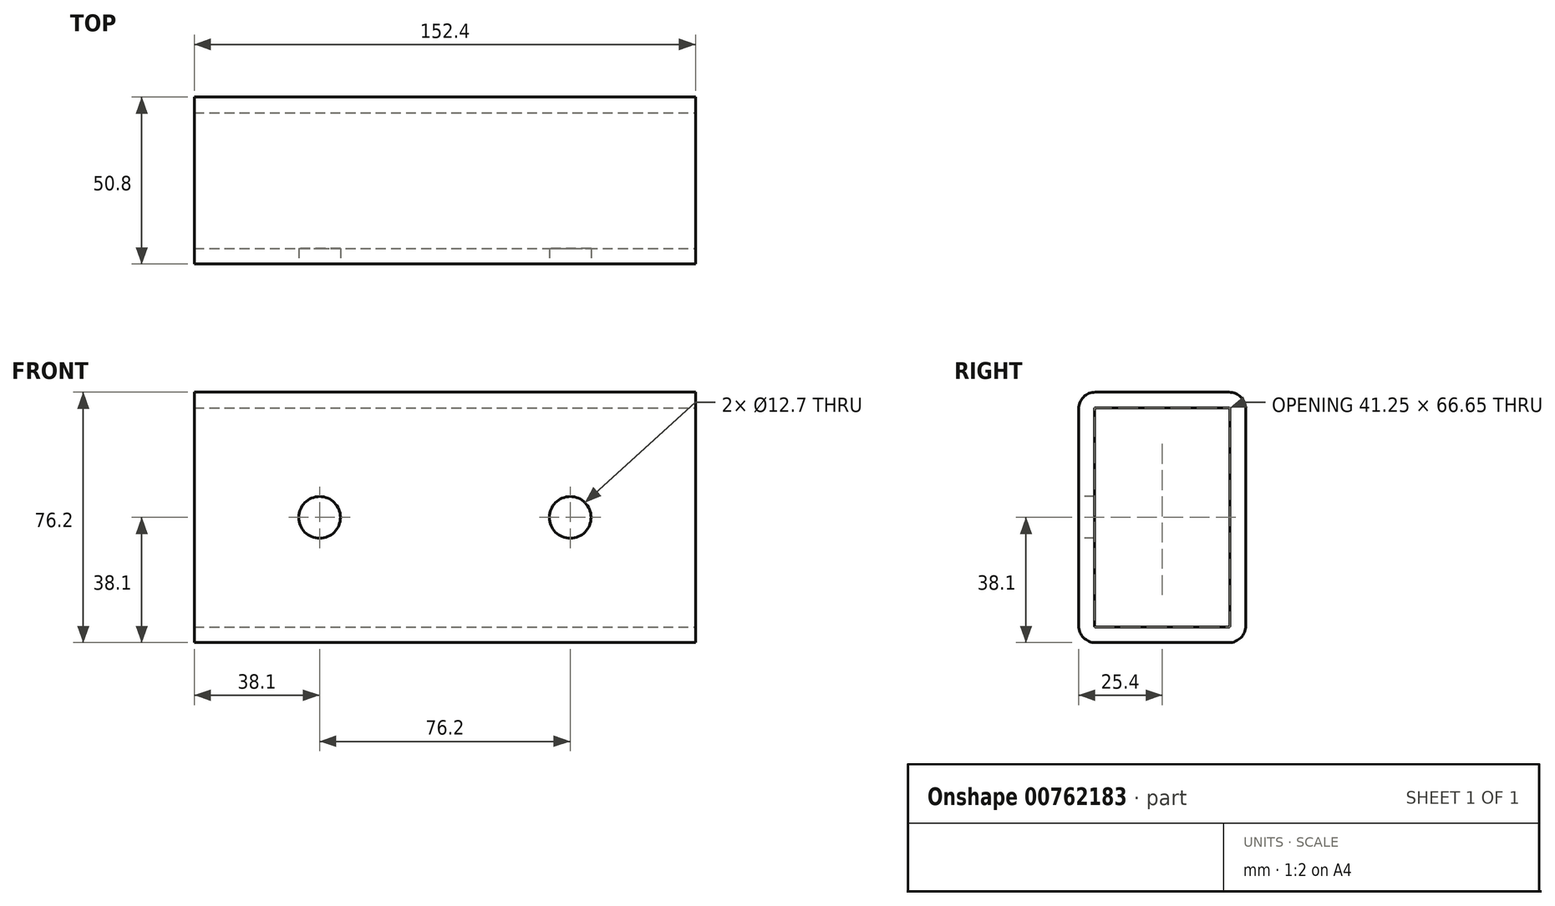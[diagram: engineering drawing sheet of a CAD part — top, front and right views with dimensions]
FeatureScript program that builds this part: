
annotation { "Feature Type Name" : "Feature", "Feature Type Description" : "" }
export const myFeature = defineFeature(function(context is Context, id is Id, definition is map)
    precondition{}
    {
        {
            var Q0;
            Q0=qCreatedBy(makeId("Right.planeOp"),FACE);
            var sketch = newSketch(context, id + "F0", { "sketchPlane" : qUnion([Q0])});
            skLineSegment(sketch, "E0.bottom", {"start": v(0, 0) * mm, "end": v(50.8, 0) * mm});
            skLineSegment(sketch, "E0.top", {"start": v(0, 76.2) * mm, "end": v(50.8, 76.2) * mm});
            skLineSegment(sketch, "E0.left", {"start": v(0, 0) * mm, "end": v(0, 76.2) * mm});
            skLineSegment(sketch, "E0.right", {"start": v(50.8, 0) * mm, "end": v(50.8, 76.2) * mm});
            skSolve(sketch);
        }
        {
            var Q0;
            Q0=makeQuery(id+"F0.imprint","IMPRINT",FACE,{"disambiguationData":[TD([[makeQuery(id+"F0.imprint","IMPRINT",EDGE,{"derivedFrom":sQuery(id+"F0.wireOp",EDGE,"E0.bottom")}),1.0]])]});
            extrude(context, id + "F1", {"entities" : qUnion([Q0]), "depth" : 152.4 * mm, "offsetDistance" : 25.4 * mm});
        }
        {
            var Q0;
            Q0=makeQuery(id+"F1.opExtrude","SWEPT_EDGE",EDGE,{"disambiguationData":[OSD([sQuery(id+"F0.wireOp",EDGE,"E0.top"),sQuery(id+"F0.wireOp",EDGE,"E0.left")])]});
            var Q1;
            Q1=makeQuery(id+"F1.opExtrude","SWEPT_EDGE",EDGE,{"disambiguationData":[OSD([sQuery(id+"F0.wireOp",EDGE,"E0.top"),sQuery(id+"F0.wireOp",EDGE,"E0.right")])]});
            var Q2;
            Q2=makeQuery(id+"F1.opExtrude","SWEPT_EDGE",EDGE,{"disambiguationData":[OSD([sQuery(id+"F0.wireOp",EDGE,"E0.bottom"),sQuery(id+"F0.wireOp",EDGE,"E0.left")])]});
            var Q3;
            Q3=makeQuery(id+"F1.opExtrude","SWEPT_EDGE",EDGE,{"disambiguationData":[OSD([sQuery(id+"F0.wireOp",EDGE,"E0.bottom"),sQuery(id+"F0.wireOp",EDGE,"E0.right")])]});
            fillet(context, id + "F2", {"entities" : qUnion([Q0, Q1, Q2, Q3]), "radius" : 5.08 * mm, "tangentPropagation" : true, "allowEdgeOverflow" : false});
        }
        {
            var Q0;
            Q0=makeQuery(id+"F1.opExtrude","CAP_FACE",FACE,{"disambiguationData":[OSD([sQuery(id+"F0.wireOp",EDGE,"E0.bottom"),sQuery(id+"F0.wireOp",EDGE,"E0.top"),sQuery(id+"F0.wireOp",EDGE,"E0.left"),sQuery(id+"F0.wireOp",EDGE,"E0.right")])],"isStart":false});
            var Q1;
            Q1=makeQuery(id+"F1.opExtrude","CAP_FACE",FACE,{"disambiguationData":[OSD([sQuery(id+"F0.wireOp",EDGE,"E0.bottom"),sQuery(id+"F0.wireOp",EDGE,"E0.top"),sQuery(id+"F0.wireOp",EDGE,"E0.left"),sQuery(id+"F0.wireOp",EDGE,"E0.right")])],"isStart":true});
            shell(context, id + "F3", {"entities" : qUnion([Q0, Q1]), "thickness" : 4.78 * mm});
        }
        {
            var Q0;
            Q0=makeQuery(id+"F1.opExtrude","SWEPT_FACE",FACE,{"disambiguationData":[OSD([sQuery(id+"F0.wireOp",EDGE,"E0.left")])]});
            var sketch = newSketch(context, id + "F4", { "sketchPlane" : qUnion([Q0])});
            skCircle(sketch, "E1", {"center": v(38.1, 38.1) * mm, "radius": 6.35 * mm});
            skPoint(sketch, "E1.centerSnap0", {"position": v(0, 38.1) * mm});
            skCircle(sketch, "E2", {"center": v(114.3, 38.1) * mm, "radius": 6.35 * mm});
            skSolve(sketch);
        }
        {
            var Q0;
            Q0=makeQuery(id+"F4.imprint","IMPRINT",FACE,{"disambiguationData":[TD([[makeQuery(id+"F4.imprint","IMPRINT",EDGE,{"derivedFrom":sQuery(id+"F4.wireOp",EDGE,"E1")}),1.0]])]});
            var Q1;
            Q1=makeQuery(id+"F4.imprint","IMPRINT",FACE,{"disambiguationData":[TD([[makeQuery(id+"F4.imprint","IMPRINT",EDGE,{"derivedFrom":sQuery(id+"F4.wireOp",EDGE,"E2")}),1.0]])]});
            extrude(context, id + "F5", {"entities" : qUnion([Q0, Q1]), "operationType" : NewBodyOperationType.REMOVE, "endBound" : BoundingType.UP_TO_NEXT, "oppositeDirection" : true, "depth" : 25.4 * mm, "offsetDistance" : 25.4 * mm});
        }
    });
